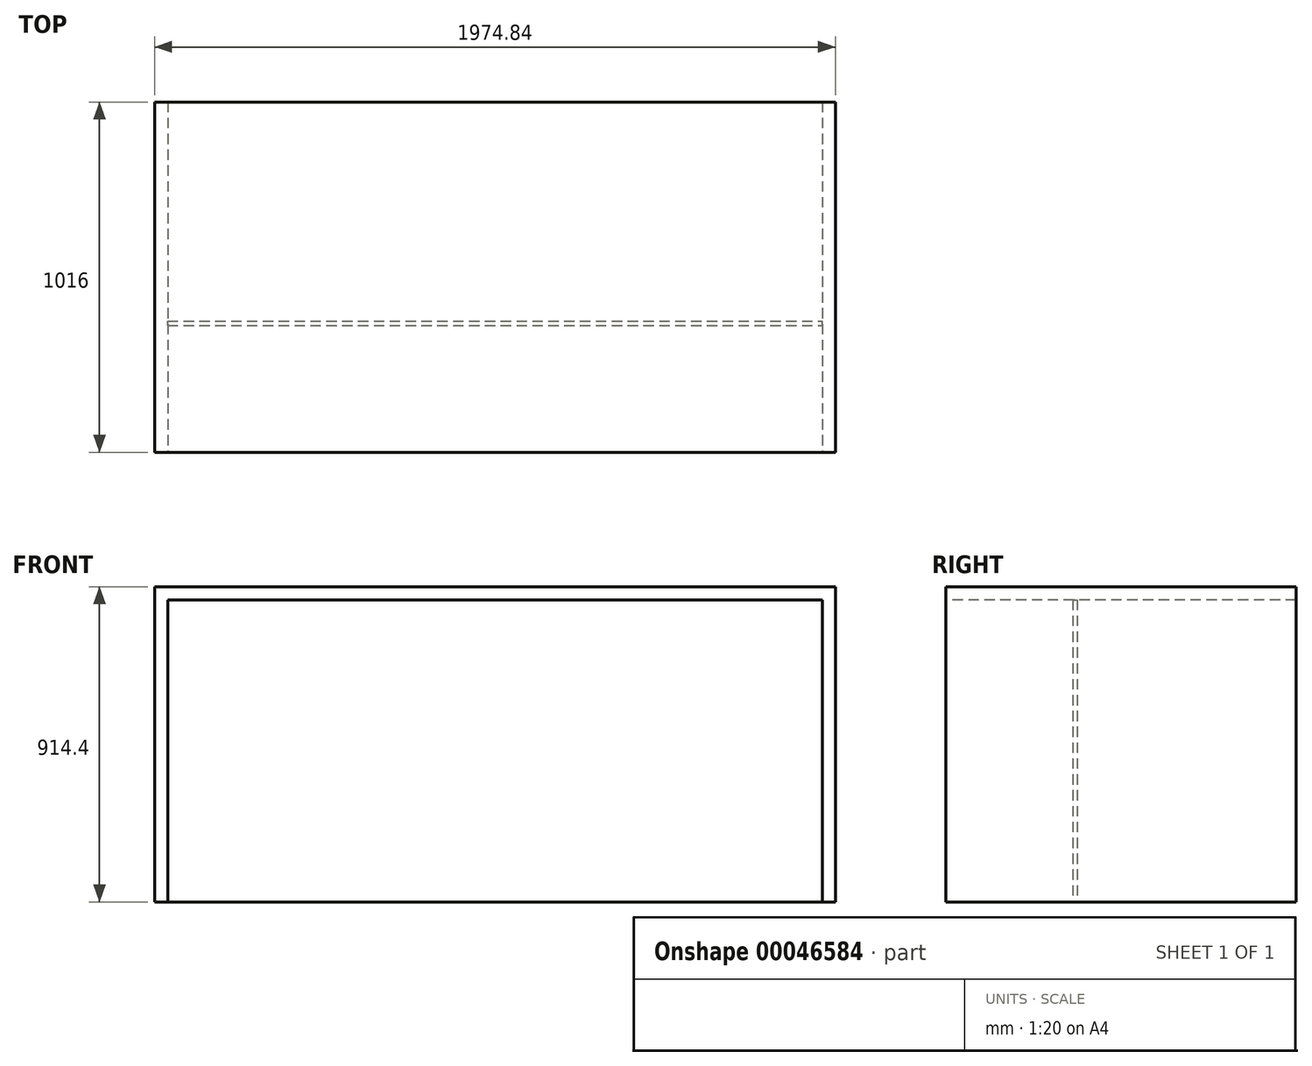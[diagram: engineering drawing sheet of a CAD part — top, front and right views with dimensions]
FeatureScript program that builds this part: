
annotation { "Feature Type Name" : "Feature", "Feature Type Description" : "" }
export const myFeature = defineFeature(function(context is Context, id is Id, definition is map)
    precondition{}
    {
        {
            var Q0;
            Q0=qCreatedBy(makeId("Top.planeOp"),FACE);
            var sketch = newSketch(context, id + "F0", { "sketchPlane" : qUnion([Q0])});
            skLineSegment(sketch, "E0.rect.bottom", {"start": v(949.33, 508) * mm, "end": v(-949.33, 508) * mm});
            skLineSegment(sketch, "E0.rect.top", {"start": v(949.33, -508) * mm, "end": v(-949.32, -508) * mm});
            skLineSegment(sketch, "E0.rect.left", {"start": v(949.32, 508) * mm, "end": v(949.33, -508) * mm});
            skLineSegment(sketch, "E0.rect.right", {"start": v(-949.33, 508) * mm, "end": v(-949.32, -508) * mm});
            skPoint(sketch, "E0.rect.middle", {"position": v(0, 0) * mm});
            skLineSegment(sketch, "E1.bottom", {"start": v(-949.33, 508) * mm, "end": v(-987.43, 508) * mm});
            skLineSegment(sketch, "E1.top", {"start": v(-949.32, -508) * mm, "end": v(-987.42, -508) * mm});
            skLineSegment(sketch, "E1.right", {"start": v(-987.43, 508) * mm, "end": v(-987.43, -508) * mm});
            skLineSegment(sketch, "E2.bottom", {"start": v(949.33, 508) * mm, "end": v(987.43, 508) * mm});
            skLineSegment(sketch, "E2.top", {"start": v(949.33, -508) * mm, "end": v(987.43, -508) * mm});
            skLineSegment(sketch, "E2.left", {"start": v(949.33, 508) * mm, "end": v(949.33, -508) * mm});
            skLineSegment(sketch, "E2.right", {"start": v(987.42, 508) * mm, "end": v(987.42, -508) * mm});
            skSolve(sketch);
        }
        {
            var Q0;
            Q0=makeQuery(id+"F0.imprint","IMPRINT",FACE,{"disambiguationData":[TD([[makeQuery(id+"F0.imprint","IMPRINT",EDGE,{"derivedFrom":sQuery(id+"F0.wireOp",EDGE,"E1.bottom")}),1.0]])]});
            var Q1;
            Q1=makeQuery(id+"F0.imprint","IMPRINT",FACE,{"disambiguationData":[TD([[makeQuery(id+"F0.imprint","IMPRINT",EDGE,{"derivedFrom":sQuery(id+"F0.wireOp",EDGE,"E0.rect.bottom")}),1.0]])]});
            var Q2;
            Q2=makeQuery(id+"F0.imprint","IMPRINT",FACE,{"disambiguationData":[TD([[makeQuery(id+"F0.imprint","IMPRINT",EDGE,{"derivedFrom":sQuery(id+"F0.wireOp",EDGE,"E2.bottom")}),-1.0]])]});
            extrude(context, id + "F1", {"entities" : qUnion([Q0, Q1, Q2]), "depth" : 38.1 * mm});
        }
        {
            var Q0;
            Q0=makeQuery(id+"F0.imprint","IMPRINT",FACE,{"disambiguationData":[TD([[makeQuery(id+"F0.imprint","IMPRINT",EDGE,{"derivedFrom":sQuery(id+"F0.wireOp",EDGE,"E1.bottom")}),1.0]])]});
            var Q1;
            Q1=makeQuery(id+"F0.imprint","IMPRINT",FACE,{"disambiguationData":[TD([[makeQuery(id+"F0.imprint","IMPRINT",EDGE,{"derivedFrom":sQuery(id+"F0.wireOp",EDGE,"E2.bottom")}),-1.0]])]});
            extrude(context, id + "F2", {"entities" : qUnion([Q0, Q1]), "operationType" : NewBodyOperationType.ADD, "oppositeDirection" : true, "depth" : 876.3 * mm});
        }
        {
            var Q0;
            {var subQ0=sQuery(id+"F0.wireOp",EDGE,"E2.top");var subQ1=sQuery(id+"F0.wireOp",EDGE,"E1.top");Q0=makeQuery(id+"F2.boolean.opBoolean","MERGE",FACE,{"derivedFrom":[makeQuery(id+"F1.opExtrude","SWEPT_FACE",FACE,{"disambiguationData":[OSD([sQuery(id+"F0.wireOp",EDGE,"E0.rect.top"),subQ1,subQ0])]}),makeQuery(id+"F2.opExtrude","SWEPT_FACE",FACE,{"disambiguationData":[OSD([subQ1])]}),makeQuery(id+"F2.opExtrude","SWEPT_FACE",FACE,{"disambiguationData":[OSD([subQ0])]})]});}
            cPlane(context, id + "F3", {"entities" : qUnion([Q0]), "cplaneType" : CPlaneType.OFFSET, "offset" : 381 * mm, "oppositeDirection" : true, "width" : 152.4 * mm, "height" : 152.4 * mm});
        }
        {
            var Q0;
            Q0=qCreatedBy(id+"F3.planeOp",FACE);
            var sketch = newSketch(context, id + "F4", { "sketchPlane" : qUnion([Q0])});
            skLineSegment(sketch, "E3.bottom", {"start": v(-949.32, 0) * mm, "end": v(949.33, 0) * mm});
            skLineSegment(sketch, "E3.top", {"start": v(-949.32, -876.3) * mm, "end": v(949.33, -876.3) * mm});
            skLineSegment(sketch, "E3.left", {"start": v(-949.32, 0) * mm, "end": v(-949.32, -876.3) * mm});
            skLineSegment(sketch, "E3.right", {"start": v(949.33, 0) * mm, "end": v(949.33, -876.3) * mm});
            skSolve(sketch);
        }
        {
            var Q0;
            Q0 = qSketchRegion(id + "F4", true);
            extrude(context, id + "F5", {"entities" : qUnion([Q0]), "depth" : 12.7 * mm});
        }
    });
